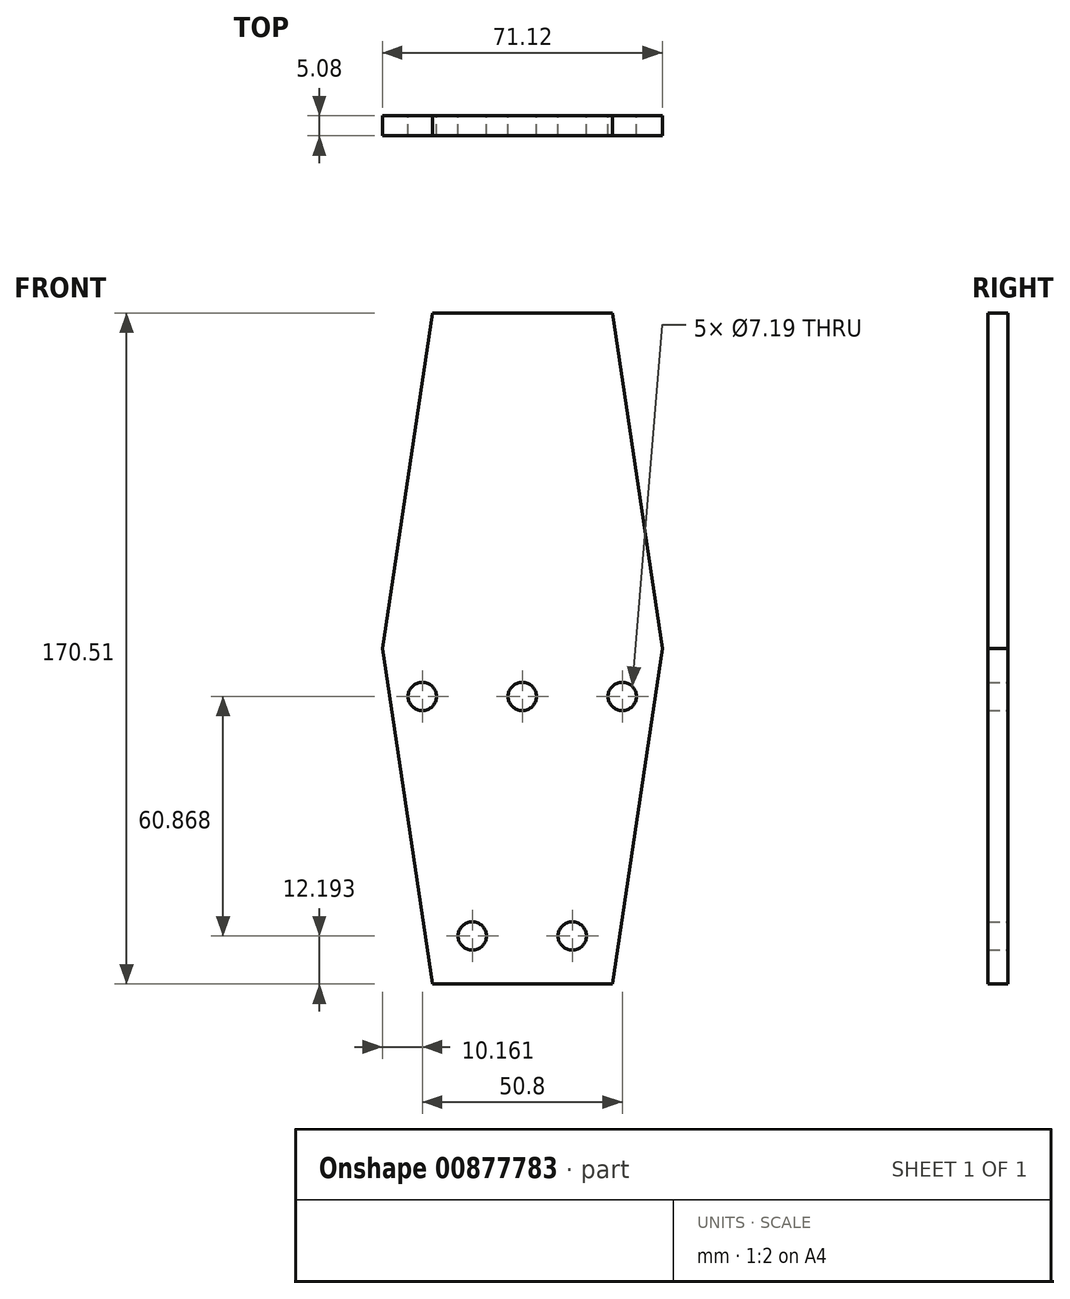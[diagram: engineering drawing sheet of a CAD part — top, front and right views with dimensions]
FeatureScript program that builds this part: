
annotation { "Feature Type Name" : "Feature", "Feature Type Description" : "" }
export const myFeature = defineFeature(function(context is Context, id is Id, definition is map)
    precondition{}
    {
        {
            var Q0;
            Q0=qCreatedBy(makeId("Front.planeOp"),FACE);
            var sketch = newSketch(context, id + "F0", { "sketchPlane" : qUnion([Q0])});
            skCircle(sketch, "E0", {"center": v(-45.2, -33.32) * mm, "radius": 3.6 * mm});
            skCircle(sketch, "E1", {"center": v(-19.8, -33.32) * mm, "radius": 3.6 * mm});
            skLineSegment(sketch, "E2", {"start": v(-45.2, -45.51) * mm, "end": v(-19.8, -45.51) * mm});
            skLineSegment(sketch, "E3", {"start": v(-45.2, -45.51) * mm, "end": v(-55.36, -45.51) * mm});
            skLineSegment(sketch, "E4", {"start": v(-19.8, -45.51) * mm, "end": v(-9.64, -45.51) * mm});
            skCircle(sketch, "E5", {"center": v(-32.5, 27.55) * mm, "radius": 3.6 * mm});
            skCircle(sketch, "E6", {"center": v(-57.9, 27.55) * mm, "radius": 3.6 * mm});
            skCircle(sketch, "E7", {"center": v(-7.1, 27.55) * mm, "radius": 3.6 * mm});
            skLineSegment(sketch, "E8", {"start": v(-68.06, 39.74) * mm, "end": v(-55.36, -45.51) * mm});
            skLineSegment(sketch, "E9", {"start": v(3.06, 39.74) * mm, "end": v(-9.64, -45.51) * mm});
            skLineSegment(sketch, "E10.MirrorCS", {"start": v(-68.06, 39.74) * mm, "end": v(-55.36, 125) * mm});
            skLineSegment(sketch, "E11.MirrorCS", {"start": v(-45.2, 125) * mm, "end": v(-55.36, 125) * mm});
            skLineSegment(sketch, "E12.MirrorCS", {"start": v(-45.2, 125) * mm, "end": v(-19.8, 125) * mm});
            skLineSegment(sketch, "E13.MirrorCS", {"start": v(-19.8, 125) * mm, "end": v(-9.64, 125) * mm});
            skLineSegment(sketch, "E14.MirrorCS", {"start": v(3.06, 39.74) * mm, "end": v(-9.64, 125) * mm});
            skSolve(sketch);
        }
        {
            var Q0;
            Q0 = qSketchRegion(id + "F0", true);
            extrude(context, id + "F1", {"entities" : qUnion([Q0]), "depth" : 5.08 * mm, "offsetDistance" : 25.4 * mm});
        }
    });
